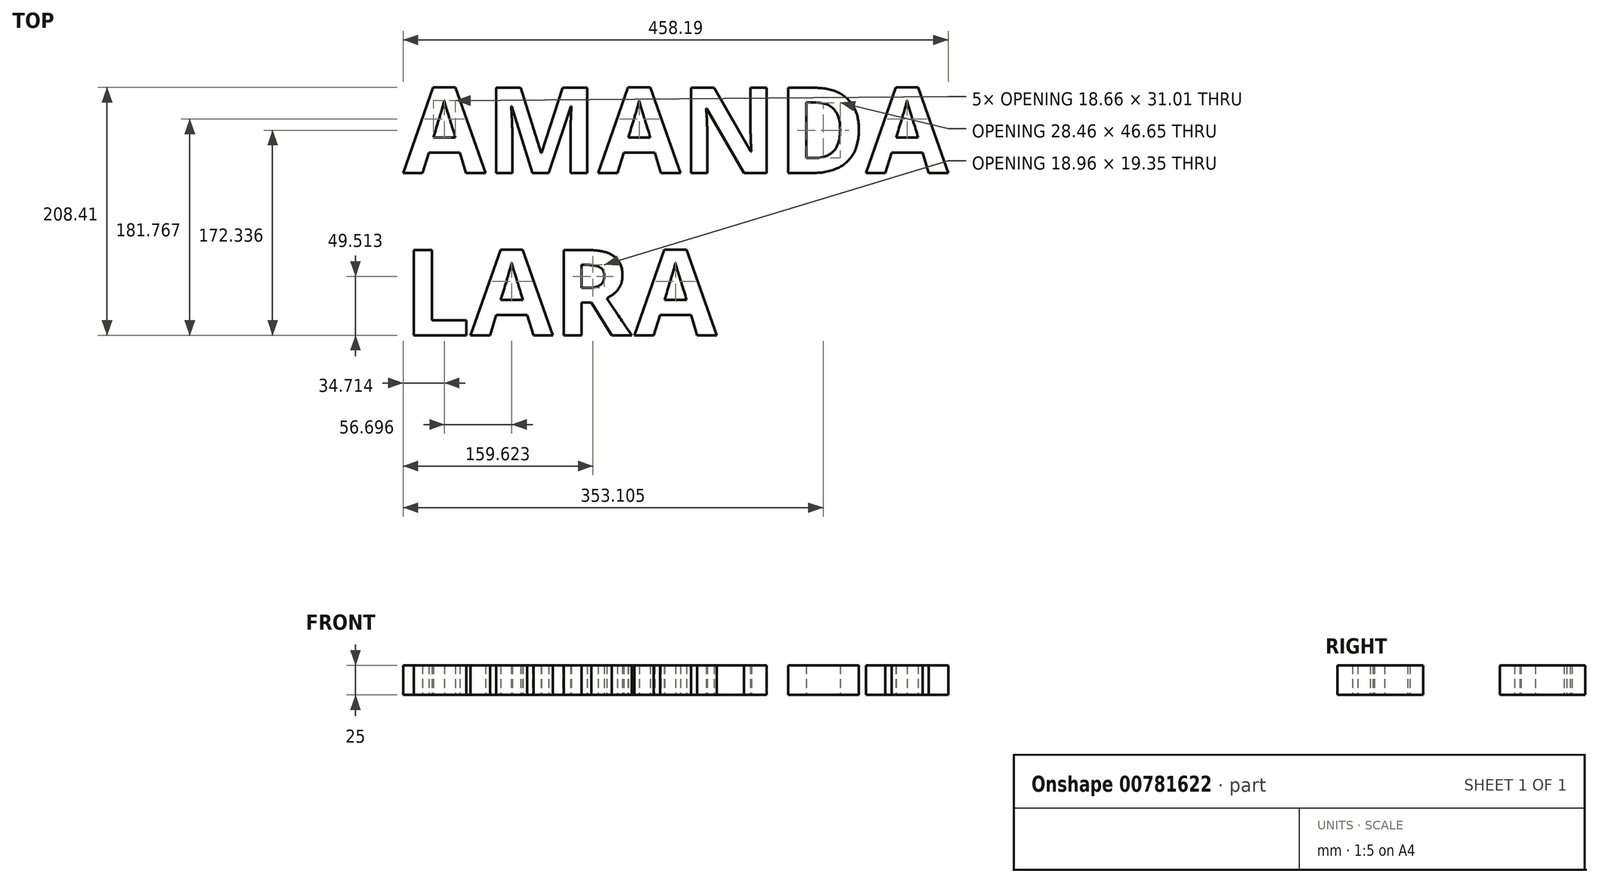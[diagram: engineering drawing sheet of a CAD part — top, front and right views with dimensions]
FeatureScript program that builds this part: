
annotation { "Feature Type Name" : "Feature", "Feature Type Description" : "" }
export const myFeature = defineFeature(function(context is Context, id is Id, definition is map)
    precondition{}
    {
        {
            var Q0;
            Q0=qCreatedBy(makeId("Top.planeOp"),FACE);
            var sketch = newSketch(context, id + "F0", { "sketchPlane" : qUnion([Q0])});
            skText(sketch, "E0", { "text": "AMANDA\nLARA", "fontName": "OpenSans-Bold.ttf"});
            const initialGuessF0  = {"E0": [-0.06484, -0.03594, 1, 0, 0.07225]};
            skSetInitialGuess(sketch, initialGuessF0);
            skSolve(sketch);
        }
        {
            var Q0;
            Q0 = qSketchRegion(id + "F0", true);
            extrude(context, id + "F1", {"entities" : qUnion([Q0]), "depth" : 25 * mm, "offsetDistance" : 25 * mm});
        }
    });
